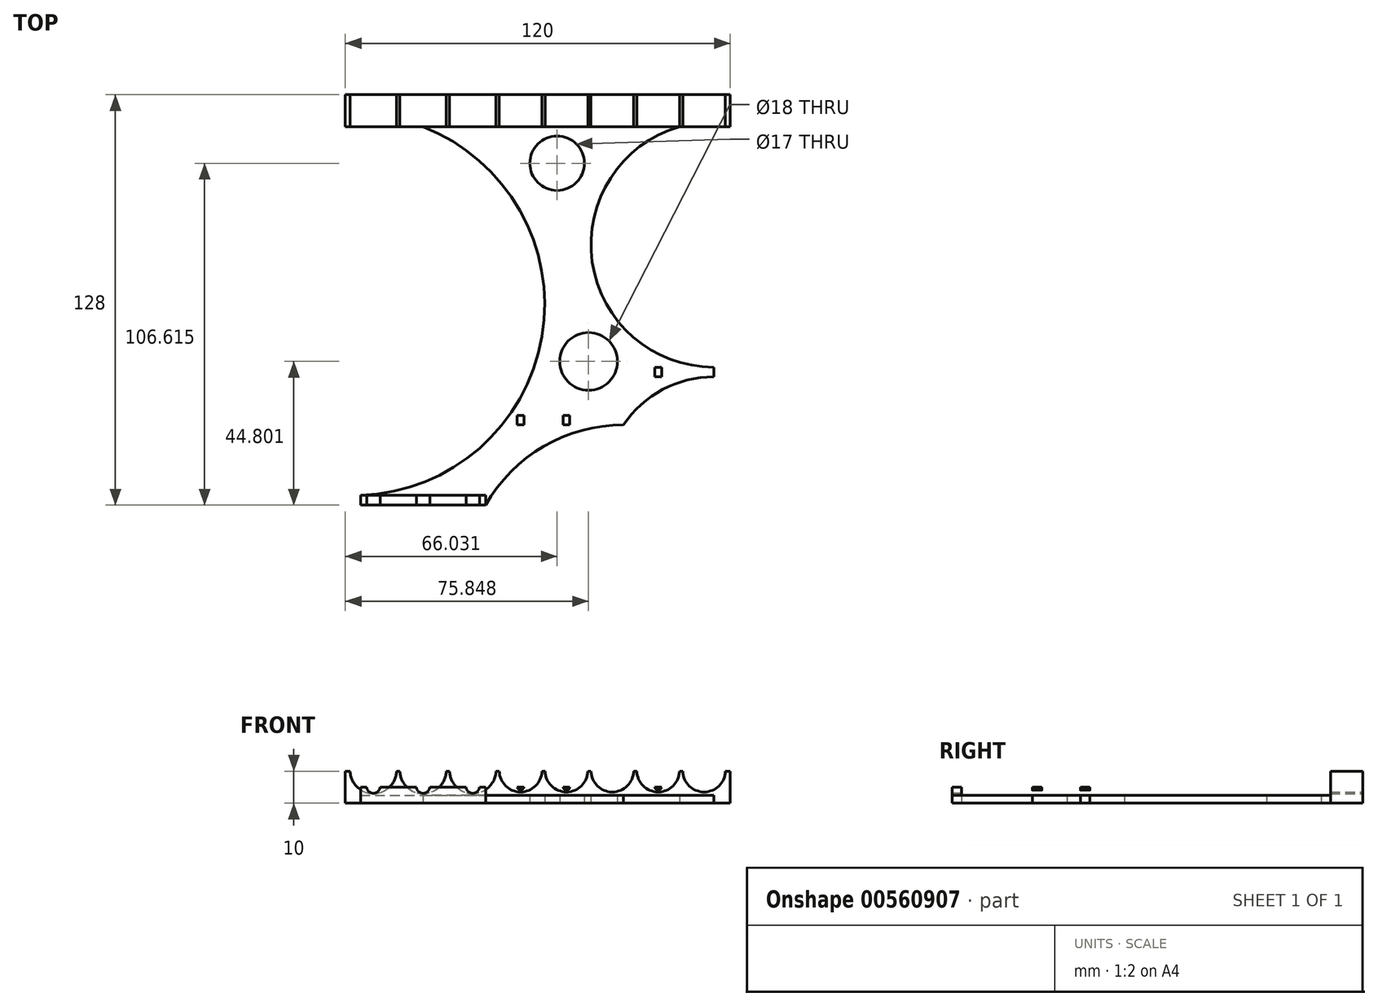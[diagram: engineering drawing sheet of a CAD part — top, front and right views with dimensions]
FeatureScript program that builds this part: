
annotation { "Feature Type Name" : "Feature", "Feature Type Description" : "" }
export const myFeature = defineFeature(function(context is Context, id is Id, definition is map)
    precondition{}
    {
        {
            var Q0;
            Q0=qCreatedBy(makeId("Top.planeOp"),FACE);
            var sketch = newSketch(context, id + "F0", { "sketchPlane" : qUnion([Q0])});
            skLineSegment(sketch, "E0.top", {"start": v(-60, -5) * mm, "end": v(60, -5) * mm});
            skLineSegment(sketch, "E0.left", {"start": v(-60, 5) * mm, "end": v(-60, -5) * mm});
            skLineSegment(sketch, "E0.right", {"start": v(60, 5) * mm, "end": v(60, -5) * mm});
            skPoint(sketch, "E0.middle", {"position": v(0, 0) * mm});
            skLineSegment(sketch, "E1", {"start": v(0, 5) * mm, "end": v(0, -5) * mm, "construction": true});
            skLineSegment(sketch, "E2", {"start": v(0, 5) * mm, "end": v(0, -120) * mm, "construction": true});
            skLineSegment(sketch, "E3", {"start": v(-60, 0) * mm, "end": v(60, 0) * mm, "construction": true});
            skLineSegment(sketch, "E4", {"start": v(-60, -5) * mm, "end": v(-60, -120) * mm, "construction": true});
            skLineSegment(sketch, "E5", {"start": v(-58.5, 5) * mm, "end": v(-58.5, -5) * mm, "construction": true});
            skLineSegment(sketch, "E6", {"start": v(58.5, 5) * mm, "end": v(58.5, -5) * mm, "construction": true});
            skLineSegment(sketch, "E7", {"start": v(-44, 5) * mm, "end": v(-44, -5) * mm, "construction": true});
            skLineSegment(sketch, "E8", {"start": v(-28.5, 5) * mm, "end": v(-28.5, -5) * mm, "construction": true});
            skLineSegment(sketch, "E9", {"start": v(-13, 5) * mm, "end": v(-13, -5) * mm, "construction": true});
            skLineSegment(sketch, "E10", {"start": v(1.3, 5) * mm, "end": v(1.3, -5) * mm, "construction": true});
            skLineSegment(sketch, "E11", {"start": v(15.6, 5) * mm, "end": v(15.6, -5) * mm, "construction": true});
            skLineSegment(sketch, "E12", {"start": v(29.9, 5) * mm, "end": v(29.9, -5) * mm, "construction": true});
            skLineSegment(sketch, "E13", {"start": v(44.2, 5) * mm, "end": v(44.2, -5) * mm, "construction": true});
            skLineSegment(sketch, "E14", {"start": v(-43, 5) * mm, "end": v(-43, -5) * mm, "construction": true});
            skLineSegment(sketch, "E15", {"start": v(-27.5, 5) * mm, "end": v(-27.5, -5) * mm, "construction": true});
            skLineSegment(sketch, "E16", {"start": v(-12, 5) * mm, "end": v(-12, -5) * mm, "construction": true});
            skLineSegment(sketch, "E17", {"start": v(2.3, 5) * mm, "end": v(2.3, -5) * mm, "construction": true});
            skLineSegment(sketch, "E18", {"start": v(16.6, 5) * mm, "end": v(16.6, -5) * mm, "construction": true});
            skLineSegment(sketch, "E19", {"start": v(30.9, 5) * mm, "end": v(30.9, -5) * mm, "construction": true});
            skLineSegment(sketch, "E20", {"start": v(45.2, 5) * mm, "end": v(45.2, -5) * mm, "construction": true});
            skLineSegment(sketch, "E21", {"start": v(-51.25, 5) * mm, "end": v(-51.25, -120) * mm, "construction": true});
            skLineSegment(sketch, "E22", {"start": v(-35.75, 5) * mm, "end": v(-35.75, -120) * mm, "construction": true});
            skLineSegment(sketch, "E23", {"start": v(-20.25, 5) * mm, "end": v(-20.25, -120) * mm, "construction": true});
            skLineSegment(sketch, "E24", {"start": v(60, -5) * mm, "end": v(60, -120) * mm, "construction": true});
            skLineSegment(sketch, "E25", {"start": v(-60, -120) * mm, "end": v(60, -120) * mm, "construction": true});
            skLineSegment(sketch, "E26", {"start": v(-5.35, 5) * mm, "end": v(-5.35, -120) * mm, "construction": true});
            skLineSegment(sketch, "E27", {"start": v(8.95, 5) * mm, "end": v(8.95, -120) * mm, "construction": true});
            skLineSegment(sketch, "E28", {"start": v(23.25, 5) * mm, "end": v(23.25, -120) * mm, "construction": true});
            skLineSegment(sketch, "E29", {"start": v(37.55, 5) * mm, "end": v(37.55, -120) * mm, "construction": true});
            skLineSegment(sketch, "E30", {"start": v(51.85, 5) * mm, "end": v(51.85, -120) * mm, "construction": true});
            skLineSegment(sketch, "E31", {"start": v(-58.5, 5) * mm, "end": v(-44, 5) * mm});
            skLineSegment(sketch, "E32", {"start": v(-43, 5) * mm, "end": v(-28.5, 5) * mm});
            skLineSegment(sketch, "E33", {"start": v(-27.5, 5) * mm, "end": v(-13, 5) * mm});
            skLineSegment(sketch, "E34", {"start": v(-12, 5) * mm, "end": v(1.3, 5) * mm});
            skLineSegment(sketch, "E35", {"start": v(2.3, 5) * mm, "end": v(15.6, 5) * mm});
            skLineSegment(sketch, "E36", {"start": v(16.6, 5) * mm, "end": v(29.9, 5) * mm});
            skLineSegment(sketch, "E37", {"start": v(30.9, 5) * mm, "end": v(44.2, 5) * mm});
            skLineSegment(sketch, "E38", {"start": v(45.2, 5) * mm, "end": v(58.5, 5) * mm});
            skLineSegment(sketch, "E39", {"start": v(-60, 5) * mm, "end": v(60, 5) * mm});
            skLineSegment(sketch, "E40", {"start": v(-60, -95) * mm, "end": v(60, -95) * mm, "construction": true});
            skLineSegment(sketch, "E41", {"start": v(-60, -80) * mm, "end": v(60, -80) * mm, "construction": true});
            skLineSegment(sketch, "E42", {"start": v(-55.25, -120) * mm, "end": v(-55.25, -123) * mm, "construction": true});
            skLineSegment(sketch, "E43", {"start": v(-39.75, -120) * mm, "end": v(-39.75, -123) * mm, "construction": true});
            skLineSegment(sketch, "E44", {"start": v(-24.25, -120) * mm, "end": v(-24.25, -123) * mm, "construction": true});
            skLineSegment(sketch, "E45", {"start": v(-8.85, -95) * mm, "end": v(-8.85, -98) * mm, "construction": true});
            skLineSegment(sketch, "E46", {"start": v(5.45, -95) * mm, "end": v(5.45, -98) * mm, "construction": true});
            skLineSegment(sketch, "E47", {"start": v(19.75, -95) * mm, "end": v(19.75, -98) * mm, "construction": true});
            skLineSegment(sketch, "E48", {"start": v(34.55, -80) * mm, "end": v(34.55, -83) * mm, "construction": true});
            skLineSegment(sketch, "E49", {"start": v(48.85, -80) * mm, "end": v(48.85, -83) * mm, "construction": true});
            skLineSegment(sketch, "E50.MirrorCS", {"start": v(54.85, -80) * mm, "end": v(54.85, -83) * mm, "construction": true});
            skLineSegment(sketch, "E51.MirrorCS", {"start": v(40.55, -80) * mm, "end": v(40.55, -83) * mm, "construction": true});
            skLineSegment(sketch, "E52.bottom", {"start": v(34.55, -83) * mm, "end": v(54.85, -83) * mm});
            skLineSegment(sketch, "E52.top", {"start": v(34.55, -80) * mm, "end": v(54.85, -80) * mm});
            skLineSegment(sketch, "E52.left", {"start": v(34.55, -83) * mm, "end": v(34.55, -80) * mm});
            skLineSegment(sketch, "E52.right", {"start": v(54.85, -83) * mm, "end": v(54.85, -80) * mm});
            skLineSegment(sketch, "E53.MirrorCS", {"start": v(26.75, -95) * mm, "end": v(26.75, -98) * mm, "construction": true});
            skLineSegment(sketch, "E54.MirrorCS", {"start": v(12.45, -95) * mm, "end": v(12.45, -98) * mm, "construction": true});
            skLineSegment(sketch, "E55.MirrorCS", {"start": v(-1.85, -95) * mm, "end": v(-1.85, -98) * mm, "construction": true});
            skLineSegment(sketch, "E56.bottom", {"start": v(-8.85, -98) * mm, "end": v(26.75, -98) * mm});
            skLineSegment(sketch, "E56.top", {"start": v(-8.85, -95) * mm, "end": v(26.75, -95) * mm});
            skLineSegment(sketch, "E56.left", {"start": v(-8.85, -98) * mm, "end": v(-8.85, -95) * mm});
            skLineSegment(sketch, "E56.right", {"start": v(26.75, -98) * mm, "end": v(26.75, -95) * mm});
            skLineSegment(sketch, "E57.MirrorCS", {"start": v(-16.25, -120) * mm, "end": v(-16.25, -123) * mm, "construction": true});
            skLineSegment(sketch, "E58.MirrorCS", {"start": v(-31.75, -120) * mm, "end": v(-31.75, -123) * mm, "construction": true});
            skLineSegment(sketch, "E59.MirrorCS", {"start": v(-47.25, -120) * mm, "end": v(-47.25, -123) * mm, "construction": true});
            skLineSegment(sketch, "E60.bottom", {"start": v(-55.25, -123) * mm, "end": v(-16.25, -123) * mm});
            skLineSegment(sketch, "E60.top", {"start": v(-55.25, -120) * mm, "end": v(-16.25, -120) * mm});
            skLineSegment(sketch, "E60.left", {"start": v(-55.25, -123) * mm, "end": v(-55.25, -120) * mm});
            skLineSegment(sketch, "E60.right", {"start": v(-16.25, -123) * mm, "end": v(-16.25, -120) * mm});
            skArc(sketch, "E61", {"start": v(26.75, -98) * mm, "mid": v(1.88, -104.7) * mm, "end": v(-16.25, -123) * mm});
            skArc(sketch, "E62", {"start": v(44.2, -5) * mm, "mid": v(16.97, -47.12) * mm, "end": v(54.85, -80) * mm});
            skArc(sketch, "E63", {"start": v(54.85, -83) * mm, "mid": v(38.92, -86.98) * mm, "end": v(26.75, -98) * mm});
            skArc(sketch, "E64", {"start": v(-55.25, -120) * mm, "mid": v(1.33, -70.44) * mm, "end": v(-35.75, -5) * mm});
            skCircle(sketch, "E65", {"center": v(15.85, -78.2) * mm, "radius": 9 * mm});
            skCircle(sketch, "E66", {"center": v(6.03, -16.39) * mm, "radius": 8.5 * mm});
            skSolve(sketch);
        }
        {
            var Q0;
            {var subQ0=sQuery(id+"F0.wireOp",EDGE,"E0.left");Q0=makeQuery(id+"F0.imprint","IMPRINT",FACE,{"disambiguationData":[TD([[makeQuery(id+"F0.imprint","IMPRINT",EDGE,{"derivedFrom":subQ0}),1.0]])]});}
            extrude(context, id + "F1", {"entities" : qUnion([Q0]), "depth" : 10 * mm, "offsetDistance" : 25 * mm});
        }
        {
            var Q0;
            Q0=makeQuery(id+"F0.imprint","IMPRINT",FACE,{"disambiguationData":[TD([[makeQuery(id+"F0.imprint","IMPRINT",EDGE,{"derivedFrom":sQuery(id+"F0.wireOp",EDGE,"E52.bottom")}),-1.0]])]});
            var Q1;
            Q1=makeQuery(id+"F0.imprint","IMPRINT",FACE,{"disambiguationData":[TD([[makeQuery(id+"F0.imprint","IMPRINT",EDGE,{"derivedFrom":sQuery(id+"F0.wireOp",EDGE,"E56.bottom")}),-1.0]])]});
            var Q2;
            Q2=makeQuery(id+"F0.imprint","IMPRINT",FACE,{"disambiguationData":[TD([[makeQuery(id+"F0.imprint","IMPRINT",EDGE,{"derivedFrom":sQuery(id+"F0.wireOp",EDGE,"E56.bottom")}),1.0]])]});
            extrude(context, id + "F2", {"entities" : qUnion([Q0, Q1, Q2]), "operationType" : NewBodyOperationType.ADD, "depth" : 2.5 * mm, "offsetDistance" : 25 * mm});
        }
        {
            var Q0;
            Q0=makeQuery(id+"F0.imprint","IMPRINT",FACE,{"disambiguationData":[TD([[makeQuery(id+"F0.imprint","IMPRINT",EDGE,{"derivedFrom":sQuery(id+"F0.wireOp",EDGE,"E60.bottom")}),1.0]])]});
            var Q1;
            Q1=makeQuery(id+"F0.imprint","IMPRINT",FACE,{"disambiguationData":[TD([[makeQuery(id+"F0.imprint","IMPRINT",EDGE,{"derivedFrom":sQuery(id+"F0.wireOp",EDGE,"E56.bottom")}),1.0]])]});
            var Q2;
            Q2=makeQuery(id+"F0.imprint","IMPRINT",FACE,{"disambiguationData":[TD([[makeQuery(id+"F0.imprint","IMPRINT",EDGE,{"derivedFrom":sQuery(id+"F0.wireOp",EDGE,"E52.bottom")}),1.0]])]});
            extrude(context, id + "F3", {"entities" : qUnion([Q0, Q1, Q2]), "operationType" : NewBodyOperationType.ADD, "depth" : 5 * mm, "offsetDistance" : 25 * mm});
        }
        {
            var Q0;
            Q0=makeQuery(id+"F1.opExtrude","SWEPT_FACE",FACE,{"disambiguationData":[OSD([sQuery(id+"F0.wireOp",EDGE,"E39")])]});
            var sketch = newSketch(context, id + "F4", { "sketchPlane" : qUnion([Q0])});
            skLineSegment(sketch, "E67.0", {"start": v(60, 10) * mm, "end": v(-60, 10) * mm});
            skLineSegment(sketch, "E68.0", {"start": v(60, 0) * mm, "end": v(-60, 0) * mm});
            skLineSegment(sketch, "E69.0", {"start": v(60, 10) * mm, "end": v(60, 0) * mm});
            skLineSegment(sketch, "E70.0", {"start": v(-60, 10) * mm, "end": v(-60, 0) * mm});
            skPoint(sketch, "E71.0", {"position": v(-58.5, 0) * mm});
            skPoint(sketch, "E72.0", {"position": v(-54.85, 0) * mm});
            skPoint(sketch, "E73.0", {"position": v(-51.85, 0) * mm});
            skPoint(sketch, "E74.0", {"position": v(-48.85, 0) * mm});
            skPoint(sketch, "E75.0", {"position": v(-45.2, 0) * mm});
            skPoint(sketch, "E76.0", {"position": v(-44.2, 0) * mm});
            skPoint(sketch, "E77.0", {"position": v(-37.55, 0) * mm});
            skLineSegment(sketch, "E78.0", {"start": v(-16.6, 0) * mm, "end": v(-54.85, 0) * mm});
            skPoint(sketch, "E79.0", {"position": v(-34.55, 0) * mm});
            skPoint(sketch, "E80.0", {"position": v(-30.9, 0) * mm});
            skPoint(sketch, "E81.0", {"position": v(-29.9, 0) * mm});
            skPoint(sketch, "E82.0", {"position": v(-26.75, 0) * mm});
            skPoint(sketch, "E83.0", {"position": v(-23.25, 0) * mm});
            skPoint(sketch, "E84.0", {"position": v(-19.75, 0) * mm});
            skPoint(sketch, "E85.0", {"position": v(-15.85, 0) * mm});
            skPoint(sketch, "E86.0", {"position": v(-15.6, 0) * mm});
            skPoint(sketch, "E87.0", {"position": v(-12.45, 0) * mm});
            skPoint(sketch, "E88.0", {"position": v(-8.95, 0) * mm});
            skPoint(sketch, "E89.0", {"position": v(-6.03, 0) * mm});
            skPoint(sketch, "E90.0", {"position": v(-5.45, 0) * mm});
            skPoint(sketch, "E91.0", {"position": v(-2.3, 0) * mm});
            skPoint(sketch, "E92.0", {"position": v(-1.3, 0) * mm});
            skPoint(sketch, "E93.0", {"position": v(0, 0) * mm});
            skPoint(sketch, "E94.0", {"position": v(1.85, 0) * mm});
            skPoint(sketch, "E95.0", {"position": v(5.35, 0) * mm});
            skPoint(sketch, "E96.0", {"position": v(8.85, 0) * mm});
            skPoint(sketch, "E97.0", {"position": v(12, 0) * mm});
            skPoint(sketch, "E98.0", {"position": v(13, 0) * mm});
            skPoint(sketch, "E99.0", {"position": v(16.25, 0) * mm});
            skPoint(sketch, "E100.0", {"position": v(20.25, 0) * mm});
            skPoint(sketch, "E101.0", {"position": v(24.25, 0) * mm});
            skPoint(sketch, "E102.0", {"position": v(27.5, 0) * mm});
            skPoint(sketch, "E103.0", {"position": v(28.5, 0) * mm});
            skPoint(sketch, "E104.0", {"position": v(31.75, 0) * mm});
            skPoint(sketch, "E105.0", {"position": v(35.75, 0) * mm});
            skPoint(sketch, "E106.0", {"position": v(39.75, 0) * mm});
            skPoint(sketch, "E107.0", {"position": v(43, 0) * mm});
            skPoint(sketch, "E108.0", {"position": v(44, 0) * mm});
            skPoint(sketch, "E109.0", {"position": v(47.25, 0) * mm});
            skPoint(sketch, "E110.0", {"position": v(51.25, 0) * mm});
            skPoint(sketch, "E111.0", {"position": v(55.25, 0) * mm});
            skPoint(sketch, "E112.0", {"position": v(57.38, 0) * mm});
            skPoint(sketch, "E113.0", {"position": v(58.5, 0) * mm});
            skLineSegment(sketch, "E114", {"start": v(-51.85, 0) * mm, "end": v(-51.85, 10) * mm, "construction": true});
            skLineSegment(sketch, "E115", {"start": v(-37.55, 0) * mm, "end": v(-37.55, 10) * mm, "construction": true});
            skLineSegment(sketch, "E116", {"start": v(-23.25, 0) * mm, "end": v(-23.25, 10) * mm, "construction": true});
            skLineSegment(sketch, "E117", {"start": v(-8.95, 0) * mm, "end": v(-8.95, 10) * mm, "construction": true});
            skLineSegment(sketch, "E118", {"start": v(5.35, 0) * mm, "end": v(5.35, 10) * mm, "construction": true});
            skLineSegment(sketch, "E119", {"start": v(20.25, 0) * mm, "end": v(20.25, 10) * mm, "construction": true});
            skLineSegment(sketch, "E120", {"start": v(35.75, 0) * mm, "end": v(35.75, 10) * mm, "construction": true});
            skLineSegment(sketch, "E121", {"start": v(51.25, 0) * mm, "end": v(51.25, 10) * mm, "construction": true});
            skLineSegment(sketch, "E122", {"start": v(-60, 3) * mm, "end": v(60, 3) * mm, "construction": true});
            skLineSegment(sketch, "E123", {"start": v(-60, 3.5) * mm, "end": v(60, 3.5) * mm, "construction": true});
            skCircle(sketch, "E124", {"center": v(-51.85, 10.15) * mm, "radius": 6.65 * mm});
            skCircle(sketch, "E125", {"center": v(-37.55, 10.15) * mm, "radius": 6.65 * mm});
            skCircle(sketch, "E126", {"center": v(-23.25, 10.15) * mm, "radius": 6.65 * mm});
            skCircle(sketch, "E127", {"center": v(-8.95, 10.15) * mm, "radius": 6.65 * mm});
            skCircle(sketch, "E128", {"center": v(5.35, 10.15) * mm, "radius": 6.65 * mm});
            skCircle(sketch, "E129", {"center": v(20.25, 10.25) * mm, "radius": 7.25 * mm});
            skCircle(sketch, "E130", {"center": v(35.75, 10.25) * mm, "radius": 7.25 * mm});
            skCircle(sketch, "E131", {"center": v(51.25, 10.25) * mm, "radius": 7.25 * mm});
            skSolve(sketch);
        }
        {
            var Q0;
            {var subQ0=sQuery(id+"F4.wireOp",EDGE,"E124");var subQ1=sQuery(id+"F4.wireOp",EDGE,"E67.0");var subQ2=makeQuery(id+"F4.imprint","INTERSECT",VERTEX,{"disambiguationData":[OD(0.0)],"derivedFrom":[subQ1,subQ0]});Q0=makeQuery(id+"F4.imprint","IMPRINT",FACE,{"disambiguationData":[TD([[makeQuery(id+"F4.imprint","IMPRINT",EDGE,{"disambiguationData":[TD([[subQ2,-1.0]])],"derivedFrom":subQ1}),1.0]])]});}
            var Q1;
            {var subQ0=sQuery(id+"F4.wireOp",EDGE,"E125");var subQ1=sQuery(id+"F4.wireOp",EDGE,"E67.0");var subQ2=makeQuery(id+"F4.imprint","INTERSECT",VERTEX,{"disambiguationData":[OD(0.0)],"derivedFrom":[subQ1,subQ0]});Q1=makeQuery(id+"F4.imprint","IMPRINT",FACE,{"disambiguationData":[TD([[makeQuery(id+"F4.imprint","IMPRINT",EDGE,{"disambiguationData":[TD([[subQ2,-1.0]])],"derivedFrom":subQ1}),1.0]])]});}
            var Q2;
            {var subQ0=sQuery(id+"F4.wireOp",EDGE,"E126");var subQ1=sQuery(id+"F4.wireOp",EDGE,"E67.0");var subQ2=makeQuery(id+"F4.imprint","INTERSECT",VERTEX,{"disambiguationData":[OD(0.0)],"derivedFrom":[subQ1,subQ0]});Q2=makeQuery(id+"F4.imprint","IMPRINT",FACE,{"disambiguationData":[TD([[makeQuery(id+"F4.imprint","IMPRINT",EDGE,{"disambiguationData":[TD([[subQ2,-1.0]])],"derivedFrom":subQ1}),1.0]])]});}
            var Q3;
            {var subQ0=sQuery(id+"F4.wireOp",EDGE,"E127");var subQ1=sQuery(id+"F4.wireOp",EDGE,"E67.0");var subQ2=makeQuery(id+"F4.imprint","INTERSECT",VERTEX,{"disambiguationData":[OD(0.0)],"derivedFrom":[subQ1,subQ0]});Q3=makeQuery(id+"F4.imprint","IMPRINT",FACE,{"disambiguationData":[TD([[makeQuery(id+"F4.imprint","IMPRINT",EDGE,{"disambiguationData":[TD([[subQ2,-1.0]])],"derivedFrom":subQ1}),1.0]])]});}
            var Q4;
            {var subQ0=sQuery(id+"F4.wireOp",EDGE,"E128");var subQ1=sQuery(id+"F4.wireOp",EDGE,"E67.0");var subQ2=makeQuery(id+"F4.imprint","INTERSECT",VERTEX,{"disambiguationData":[OD(0.0)],"derivedFrom":[subQ1,subQ0]});Q4=makeQuery(id+"F4.imprint","IMPRINT",FACE,{"disambiguationData":[TD([[makeQuery(id+"F4.imprint","IMPRINT",EDGE,{"disambiguationData":[TD([[subQ2,-1.0]])],"derivedFrom":subQ1}),1.0]])]});}
            var Q5;
            {var subQ0=sQuery(id+"F4.wireOp",EDGE,"E129");var subQ1=sQuery(id+"F4.wireOp",EDGE,"E67.0");var subQ2=makeQuery(id+"F4.imprint","INTERSECT",VERTEX,{"disambiguationData":[OD(0.0)],"derivedFrom":[subQ1,subQ0]});Q5=makeQuery(id+"F4.imprint","IMPRINT",FACE,{"disambiguationData":[TD([[makeQuery(id+"F4.imprint","IMPRINT",EDGE,{"disambiguationData":[TD([[subQ2,-1.0]])],"derivedFrom":subQ1}),1.0]])]});}
            var Q6;
            {var subQ0=sQuery(id+"F4.wireOp",EDGE,"E130");var subQ1=sQuery(id+"F4.wireOp",EDGE,"E67.0");var subQ2=makeQuery(id+"F4.imprint","INTERSECT",VERTEX,{"disambiguationData":[OD(0.0)],"derivedFrom":[subQ1,subQ0]});Q6=makeQuery(id+"F4.imprint","IMPRINT",FACE,{"disambiguationData":[TD([[makeQuery(id+"F4.imprint","IMPRINT",EDGE,{"disambiguationData":[TD([[subQ2,-1.0]])],"derivedFrom":subQ1}),1.0]])]});}
            var Q7;
            {var subQ0=sQuery(id+"F4.wireOp",EDGE,"E131");var subQ1=sQuery(id+"F4.wireOp",EDGE,"E67.0");var subQ2=makeQuery(id+"F4.imprint","INTERSECT",VERTEX,{"disambiguationData":[OD(0.0)],"derivedFrom":[subQ1,subQ0]});Q7=makeQuery(id+"F4.imprint","IMPRINT",FACE,{"disambiguationData":[TD([[makeQuery(id+"F4.imprint","IMPRINT",EDGE,{"disambiguationData":[TD([[subQ2,-1.0]])],"derivedFrom":subQ1}),1.0]])]});}
            var Q8;
            Q8=makeQuery(id+"F1.opExtrude","SWEPT_FACE",FACE,{"disambiguationData":[OSD([sQuery(id+"F0.wireOp",EDGE,"E0.top")])]});
            extrude(context, id + "F5", {"entities" : qUnion([Q0, Q1, Q2, Q3, Q4, Q5, Q6, Q7]), "operationType" : NewBodyOperationType.REMOVE, "endBound" : BoundingType.UP_TO_SURFACE, "oppositeDirection" : true, "depth" : 25 * mm, "endBoundEntityFace" : qUnion([Q8]), "offsetDistance" : 25 * mm});
        }
        {
            var Q0;
            Q0=makeQuery(id+"F3.opExtrude","SWEPT_FACE",FACE,{"disambiguationData":[OSD([sQuery(id+"F0.wireOp",EDGE,"E60.bottom")])]});
            var sketch = newSketch(context, id + "F6", { "sketchPlane" : qUnion([Q0])});
            skLineSegment(sketch, "E132.0", {"start": v(-55.25, 0) * mm, "end": v(-16.25, 0) * mm});
            skPoint(sketch, "E133.0", {"position": v(-35.75, 5) * mm});
            skLineSegment(sketch, "E134.0", {"start": v(-55.25, 5) * mm, "end": v(-55.25, 0) * mm});
            skLineSegment(sketch, "E135.0", {"start": v(-16.25, 5) * mm, "end": v(-16.25, 2.5) * mm});
            skLineSegment(sketch, "E136.0", {"start": v(-16.25, 2.5) * mm, "end": v(-16.25, 0) * mm});
            skLineSegment(sketch, "E137.0", {"start": v(26.75, 2.5) * mm, "end": v(-8.85, 2.5) * mm});
            skLineSegment(sketch, "E138.0", {"start": v(-8.85, 5) * mm, "end": v(26.75, 5) * mm});
            skLineSegment(sketch, "E139.0", {"start": v(-8.85, 5) * mm, "end": v(-8.85, 2.5) * mm});
            skLineSegment(sketch, "E140.0", {"start": v(26.75, 5) * mm, "end": v(26.75, 2.5) * mm});
            skLineSegment(sketch, "E141.0", {"start": v(34.55, 5) * mm, "end": v(54.85, 5) * mm});
            skLineSegment(sketch, "E142.0", {"start": v(34.55, 2.5) * mm, "end": v(54.85, 2.5) * mm});
            skLineSegment(sketch, "E143.0", {"start": v(34.55, 5) * mm, "end": v(34.55, 2.5) * mm});
            skLineSegment(sketch, "E144.0", {"start": v(54.85, 5) * mm, "end": v(54.85, 2.5) * mm});
            skPoint(sketch, "E145.0", {"position": v(8.95, 0) * mm});
            skPoint(sketch, "E146.0", {"position": v(23.25, 0) * mm});
            skPoint(sketch, "E147.0", {"position": v(-5.35, 0) * mm});
            skPoint(sketch, "E148.0", {"position": v(37.55, 0) * mm});
            skPoint(sketch, "E149.0", {"position": v(51.85, 0) * mm});
            skPoint(sketch, "E150.0", {"position": v(-20.25, 0) * mm});
            skPoint(sketch, "E151.0", {"position": v(-35.75, 0) * mm});
            skPoint(sketch, "E152.0", {"position": v(-51.25, 0) * mm});
            skLineSegment(sketch, "E153.0", {"start": v(-55.25, 5) * mm, "end": v(-16.25, 5) * mm});
            skPoint(sketch, "E154.endSnap0", {"position": v(54.85, 3.75) * mm});
            skLineSegment(sketch, "E155", {"start": v(54.85, 5) * mm, "end": v(54.85, 0) * mm, "construction": true});
            skLineSegment(sketch, "E156", {"start": v(54.85, 0) * mm, "end": v(-16.25, 0) * mm, "construction": true});
            skLineSegment(sketch, "E157", {"start": v(51.85, 0) * mm, "end": v(51.85, 5) * mm, "construction": true});
            skLineSegment(sketch, "E158", {"start": v(37.55, 0) * mm, "end": v(37.55, 5) * mm, "construction": true});
            skLineSegment(sketch, "E159", {"start": v(23.25, 0) * mm, "end": v(23.25, 5) * mm, "construction": true});
            skLineSegment(sketch, "E160", {"start": v(8.95, 0) * mm, "end": v(8.95, 5) * mm, "construction": true});
            skLineSegment(sketch, "E161", {"start": v(-5.35, 0) * mm, "end": v(-5.35, 5) * mm, "construction": true});
            skLineSegment(sketch, "E162", {"start": v(-20.25, 0) * mm, "end": v(-20.25, 5) * mm, "construction": true});
            skLineSegment(sketch, "E163", {"start": v(-35.75, 0) * mm, "end": v(-35.75, 5) * mm, "construction": true});
            skLineSegment(sketch, "E164", {"start": v(-51.25, 0) * mm, "end": v(-51.25, 5) * mm, "construction": true});
            skLineSegment(sketch, "E165", {"start": v(-55.25, 3.1) * mm, "end": v(-16.25, 3.1) * mm, "construction": true});
            skLineSegment(sketch, "E166", {"start": v(-8.85, 4.1) * mm, "end": v(54.85, 4.1) * mm, "construction": true});
            skCircle(sketch, "E167", {"center": v(-51.25, 5.2) * mm, "radius": 2.1 * mm});
            skCircle(sketch, "E168", {"center": v(-35.75, 5.2) * mm, "radius": 2.1 * mm});
            skCircle(sketch, "E169", {"center": v(-20.25, 5.2) * mm, "radius": 2.1 * mm});
            skCircle(sketch, "E170", {"center": v(-5.35, 5.15) * mm, "radius": 1.05 * mm});
            skCircle(sketch, "E171", {"center": v(8.95, 5.15) * mm, "radius": 1.05 * mm});
            skCircle(sketch, "E172", {"center": v(23.25, 5.15) * mm, "radius": 1.05 * mm});
            skCircle(sketch, "E173", {"center": v(37.55, 5.15) * mm, "radius": 1.05 * mm});
            skCircle(sketch, "E174", {"center": v(51.85, 5.15) * mm, "radius": 1.05 * mm});
            skSolve(sketch);
        }
        {
            var Q0;
            {var subQ0=sQuery(id+"F6.wireOp",EDGE,"E167");var subQ1=sQuery(id+"F6.wireOp",EDGE,"E153.0");var subQ2=makeQuery(id+"F6.imprint","INTERSECT",VERTEX,{"disambiguationData":[OD(0.0)],"derivedFrom":[subQ1,subQ0]});Q0=makeQuery(id+"F6.imprint","IMPRINT",FACE,{"disambiguationData":[TD([[makeQuery(id+"F6.imprint","IMPRINT",EDGE,{"disambiguationData":[TD([[subQ2,-1.0]])],"derivedFrom":subQ1}),-1.0]])]});}
            var Q1;
            {var subQ0=sQuery(id+"F6.wireOp",EDGE,"E168");var subQ1=sQuery(id+"F6.wireOp",EDGE,"E153.0");var subQ2=makeQuery(id+"F6.imprint","INTERSECT",VERTEX,{"disambiguationData":[OD(0.0)],"derivedFrom":[subQ1,subQ0]});Q1=makeQuery(id+"F6.imprint","IMPRINT",FACE,{"disambiguationData":[TD([[makeQuery(id+"F6.imprint","IMPRINT",EDGE,{"disambiguationData":[TD([[subQ2,-1.0]])],"derivedFrom":subQ1}),-1.0]])]});}
            var Q2;
            {var subQ0=sQuery(id+"F6.wireOp",EDGE,"E169");var subQ1=sQuery(id+"F6.wireOp",EDGE,"E153.0");var subQ2=makeQuery(id+"F6.imprint","INTERSECT",VERTEX,{"disambiguationData":[OD(0.0)],"derivedFrom":[subQ1,subQ0]});Q2=makeQuery(id+"F6.imprint","IMPRINT",FACE,{"disambiguationData":[TD([[makeQuery(id+"F6.imprint","IMPRINT",EDGE,{"disambiguationData":[TD([[subQ2,-1.0]])],"derivedFrom":subQ1}),-1.0]])]});}
            var Q3;
            {var subQ0=sQuery(id+"F6.wireOp",EDGE,"E170");var subQ1=sQuery(id+"F6.wireOp",EDGE,"E138.0");var subQ2=makeQuery(id+"F6.imprint","INTERSECT",VERTEX,{"disambiguationData":[OD(0.0)],"derivedFrom":[subQ1,subQ0]});Q3=makeQuery(id+"F6.imprint","IMPRINT",FACE,{"disambiguationData":[TD([[makeQuery(id+"F6.imprint","IMPRINT",EDGE,{"disambiguationData":[TD([[subQ2,-1.0]])],"derivedFrom":subQ1}),-1.0]])]});}
            var Q4;
            {var subQ0=sQuery(id+"F6.wireOp",EDGE,"E171");var subQ1=sQuery(id+"F6.wireOp",EDGE,"E138.0");var subQ2=makeQuery(id+"F6.imprint","INTERSECT",VERTEX,{"disambiguationData":[OD(0.0)],"derivedFrom":[subQ1,subQ0]});Q4=makeQuery(id+"F6.imprint","IMPRINT",FACE,{"disambiguationData":[TD([[makeQuery(id+"F6.imprint","IMPRINT",EDGE,{"disambiguationData":[TD([[subQ2,-1.0]])],"derivedFrom":subQ1}),-1.0]])]});}
            var Q5;
            {var subQ0=sQuery(id+"F6.wireOp",EDGE,"E172");var subQ1=sQuery(id+"F6.wireOp",EDGE,"E138.0");var subQ2=makeQuery(id+"F6.imprint","INTERSECT",VERTEX,{"disambiguationData":[OD(0.0)],"derivedFrom":[subQ1,subQ0]});Q5=makeQuery(id+"F6.imprint","IMPRINT",FACE,{"disambiguationData":[TD([[makeQuery(id+"F6.imprint","IMPRINT",EDGE,{"disambiguationData":[TD([[subQ2,-1.0]])],"derivedFrom":subQ1}),-1.0]])]});}
            var Q6;
            {var subQ0=sQuery(id+"F6.wireOp",EDGE,"E173");var subQ1=sQuery(id+"F6.wireOp",EDGE,"E141.0");var subQ2=makeQuery(id+"F6.imprint","INTERSECT",VERTEX,{"disambiguationData":[OD(0.0)],"derivedFrom":[subQ1,subQ0]});Q6=makeQuery(id+"F6.imprint","IMPRINT",FACE,{"disambiguationData":[TD([[makeQuery(id+"F6.imprint","IMPRINT",EDGE,{"disambiguationData":[TD([[subQ2,-1.0]])],"derivedFrom":subQ1}),-1.0]])]});}
            var Q7;
            {var subQ0=sQuery(id+"F6.wireOp",EDGE,"E174");var subQ1=sQuery(id+"F6.wireOp",EDGE,"E141.0");var subQ2=makeQuery(id+"F6.imprint","INTERSECT",VERTEX,{"disambiguationData":[OD(0.0)],"derivedFrom":[subQ1,subQ0]});Q7=makeQuery(id+"F6.imprint","IMPRINT",FACE,{"disambiguationData":[TD([[makeQuery(id+"F6.imprint","IMPRINT",EDGE,{"disambiguationData":[TD([[subQ2,-1.0]])],"derivedFrom":subQ1}),-1.0]])]});}
            var Q8;
            Q8=makeQuery(id+"F3.opExtrude","SWEPT_FACE",FACE,{"disambiguationData":[OSD([sQuery(id+"F0.wireOp",EDGE,"E52.top")])]});
            extrude(context, id + "F7", {"entities" : qUnion([Q0, Q1, Q2, Q3, Q4, Q5, Q6, Q7]), "operationType" : NewBodyOperationType.REMOVE, "endBound" : BoundingType.UP_TO_SURFACE, "oppositeDirection" : true, "depth" : 25 * mm, "endBoundEntityFace" : qUnion([Q8]), "offsetDistance" : 25 * mm});
        }
    });
